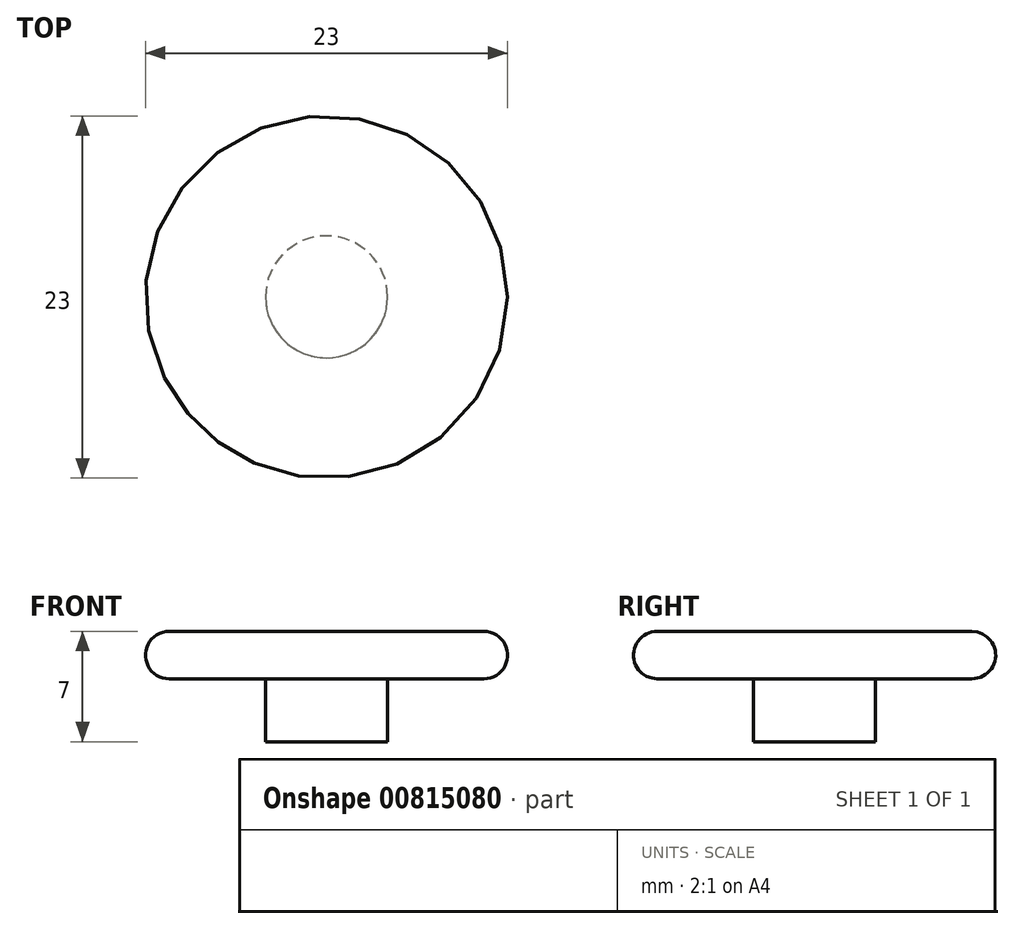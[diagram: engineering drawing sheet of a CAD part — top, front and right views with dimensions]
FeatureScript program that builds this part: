
annotation { "Feature Type Name" : "Feature", "Feature Type Description" : "" }
export const myFeature = defineFeature(function(context is Context, id is Id, definition is map)
    precondition{}
    {
        {
            var Q0;
            Q0=qCreatedBy(makeId("Top.planeOp"),FACE);
            var sketch = newSketch(context, id + "F0", { "sketchPlane" : qUnion([Q0])});
            skCircle(sketch, "E0", {"center": v(0, 0) * mm, "radius": 11.5 * mm});
            skSolve(sketch);
        }
        {
            var Q0;
            Q0=makeQuery(id+"F0.imprint","IMPRINT",FACE,{"disambiguationData":[TD([[makeQuery(id+"F0.imprint","IMPRINT",EDGE,{"derivedFrom":sQuery(id+"F0.wireOp",EDGE,"E0")}),1.0]])]});
            extrude(context, id + "F1", {"entities" : qUnion([Q0]), "depth" : 3 * mm, "offsetDistance" : 25 * mm});
        }
        {
            var Q0;
            Q0=makeQuery(id+"F1.opExtrude","CAP_EDGE",EDGE,{"disambiguationData":[OSD([sQuery(id+"F0.wireOp",EDGE,"E0")])],"isStart":false});
            fillet(context, id + "F2", {"entities" : qUnion([Q0]), "radius" : 1.5 * mm, "tangentPropagation" : true, "allowEdgeOverflow" : false});
        }
        {
            var Q0;
            Q0=makeQuery(id+"F1.opExtrude","CAP_EDGE",EDGE,{"disambiguationData":[OSD([sQuery(id+"F0.wireOp",EDGE,"E0")])],"isStart":true});
            fillet(context, id + "F3", {"entities" : qUnion([Q0]), "radius" : 1.5 * mm, "tangentPropagation" : true, "allowEdgeOverflow" : false});
        }
        {
            var Q0;
            Q0=makeQuery(id+"F1.opExtrude","CAP_FACE",FACE,{"disambiguationData":[OSD([sQuery(id+"F0.wireOp",EDGE,"E0")])],"isStart":true});
            var sketch = newSketch(context, id + "F4", { "sketchPlane" : qUnion([Q0])});
            skCircle(sketch, "E1", {"center": v(0, 0) * mm, "radius": 3.88 * mm});
            skSolve(sketch);
        }
        {
            var Q0;
            Q0=makeQuery(id+"F4.imprint","IMPRINT",FACE,{"disambiguationData":[TD([[makeQuery(id+"F4.imprint","IMPRINT",EDGE,{"derivedFrom":sQuery(id+"F4.wireOp",EDGE,"E1")}),1.0]])]});
            extrude(context, id + "F5", {"entities" : qUnion([Q0]), "operationType" : NewBodyOperationType.ADD, "depth" : 4 * mm, "offsetDistance" : 25 * mm});
        }
    });
